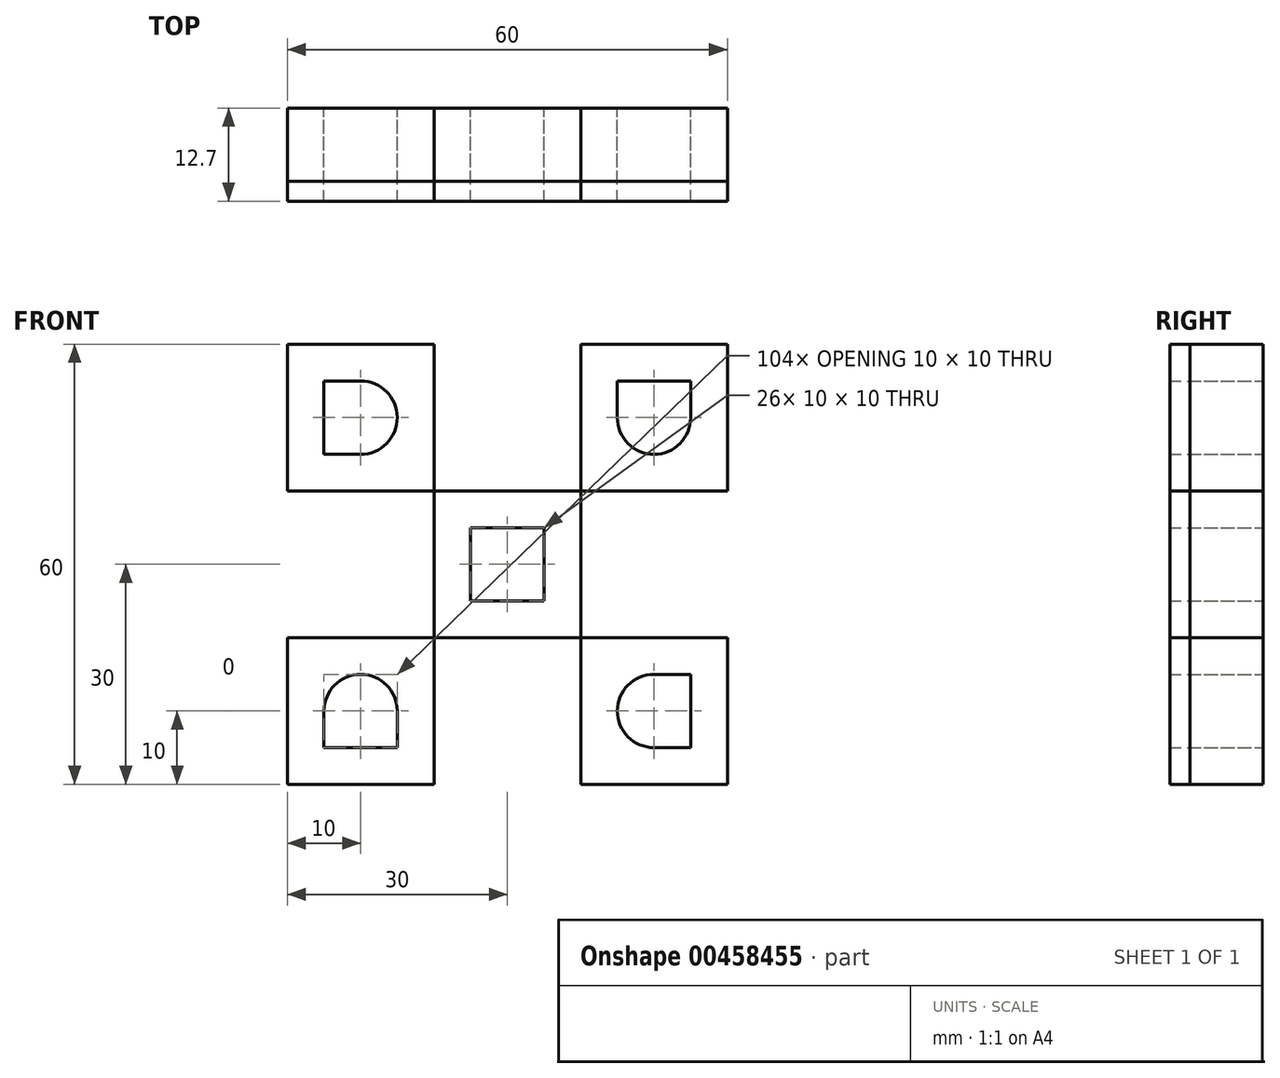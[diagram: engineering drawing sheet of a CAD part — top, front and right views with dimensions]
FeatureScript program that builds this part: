
annotation { "Feature Type Name" : "Feature", "Feature Type Description" : "" }
export const myFeature = defineFeature(function(context is Context, id is Id, definition is map)
    precondition{}
    {
        {
            var Q0;
            Q0=qCreatedBy(makeId("Front.planeOp"),FACE);
            var sketch = newSketch(context, id + "F0", { "sketchPlane" : qUnion([Q0])});
            skLineSegment(sketch, "E0.bottom", {"start": v(0, 0) * mm, "end": v(20, 0) * mm});
            skLineSegment(sketch, "E0.top", {"start": v(0, 20) * mm, "end": v(20, 20) * mm});
            skLineSegment(sketch, "E0.left", {"start": v(0, 0) * mm, "end": v(0, 20) * mm});
            skLineSegment(sketch, "E0.right", {"start": v(20, 0) * mm, "end": v(20, 20) * mm});
            skLineSegment(sketch, "E1.bottom", {"start": v(20, 20) * mm, "end": v(40, 20) * mm});
            skLineSegment(sketch, "E1.top", {"start": v(20, 40) * mm, "end": v(40, 40) * mm});
            skLineSegment(sketch, "E1.left", {"start": v(20, 20) * mm, "end": v(20, 40) * mm});
            skLineSegment(sketch, "E1.right", {"start": v(40, 20) * mm, "end": v(40, 40) * mm});
            skLineSegment(sketch, "E2.bottom", {"start": v(20, 0) * mm, "end": v(40, 0) * mm});
            skLineSegment(sketch, "E2.top", {"start": v(20, -20) * mm, "end": v(40, -20) * mm});
            skLineSegment(sketch, "E2.left", {"start": v(20, 0) * mm, "end": v(20, -20) * mm});
            skLineSegment(sketch, "E2.right", {"start": v(40, 0) * mm, "end": v(40, -20) * mm});
            skLineSegment(sketch, "E3.bottom", {"start": v(0, 0) * mm, "end": v(-20, 0) * mm});
            skLineSegment(sketch, "E3.top", {"start": v(0, -20) * mm, "end": v(-20, -20) * mm});
            skLineSegment(sketch, "E3.left", {"start": v(0, 0) * mm, "end": v(0, -20) * mm});
            skLineSegment(sketch, "E3.right", {"start": v(-20, 0) * mm, "end": v(-20, -20) * mm});
            skPoint(sketch, "E4.oppositeSnap0", {"position": v(30, 40) * mm});
            skLineSegment(sketch, "E4.bottom", {"start": v(0, 20) * mm, "end": v(-20, 20) * mm});
            skLineSegment(sketch, "E4.top", {"start": v(0, 40) * mm, "end": v(-20, 40) * mm});
            skLineSegment(sketch, "E4.left", {"start": v(0, 20) * mm, "end": v(0, 40) * mm});
            skLineSegment(sketch, "E4.right", {"start": v(-20, 20) * mm, "end": v(-20, 40) * mm});
            skLineSegment(sketch, "E5.bottom", {"start": v(15, 5) * mm, "end": v(5, 5) * mm});
            skLineSegment(sketch, "E5.top", {"start": v(15, 15) * mm, "end": v(5, 15) * mm});
            skLineSegment(sketch, "E5.left", {"start": v(15, 5) * mm, "end": v(15, 15) * mm});
            skLineSegment(sketch, "E5.right", {"start": v(5, 5) * mm, "end": v(5, 15) * mm});
            skPoint(sketch, "E5.middle", {"position": v(10, 10) * mm});
            skPoint(sketch, "E5.middle.positionSnap0", {"position": v(20, 10) * mm});
            skPoint(sketch, "E5.middle.positionSnap1", {"position": v(10, 20) * mm});
            skPoint(sketch, "E5.centerSnap0", {"position": v(20, 10) * mm});
            skPoint(sketch, "E5.centerSnap1", {"position": v(10, 20) * mm});
            skLineSegment(sketch, "E6.bottom", {"start": v(-10, 25) * mm, "end": v(-15, 25) * mm});
            skLineSegment(sketch, "E6.top", {"start": v(-10, 35) * mm, "end": v(-15, 35) * mm});
            skLineSegment(sketch, "E6.right", {"start": v(-15, 25) * mm, "end": v(-15, 35) * mm});
            skPoint(sketch, "E6.middle", {"position": v(-10, 30) * mm});
            skPoint(sketch, "E6.middle.positionSnap0", {"position": v(0, 30) * mm});
            skPoint(sketch, "E6.middle.positionSnap1", {"position": v(-10, 40) * mm});
            skPoint(sketch, "E6.centerSnap0", {"position": v(0, 30) * mm});
            skPoint(sketch, "E6.centerSnap1", {"position": v(-10, 40) * mm});
            skLineSegment(sketch, "E7.top", {"start": v(35, 35) * mm, "end": v(25, 35) * mm});
            skLineSegment(sketch, "E7.left", {"start": v(35, 30) * mm, "end": v(35, 35) * mm});
            skLineSegment(sketch, "E7.right", {"start": v(25, 30) * mm, "end": v(25, 35) * mm});
            skPoint(sketch, "E7.middle", {"position": v(30, 30) * mm});
            skPoint(sketch, "E7.middle.positionSnap0", {"position": v(40, 30) * mm});
            skPoint(sketch, "E7.centerSnap0", {"position": v(40, 30) * mm});
            skLineSegment(sketch, "E8.bottom", {"start": v(-5, -15) * mm, "end": v(-15, -15) * mm});
            skLineSegment(sketch, "E8.left", {"start": v(-5, -15) * mm, "end": v(-5, -10) * mm});
            skLineSegment(sketch, "E8.right", {"start": v(-15, -15) * mm, "end": v(-15, -10) * mm});
            skPoint(sketch, "E8.middle", {"position": v(-10, -10) * mm});
            skPoint(sketch, "E8.middle.positionSnap0", {"position": v(0, -10) * mm});
            skPoint(sketch, "E8.middle.positionSnap1", {"position": v(-10, 0) * mm});
            skPoint(sketch, "E8.centerSnap0", {"position": v(0, -10) * mm});
            skPoint(sketch, "E8.centerSnap1", {"position": v(-10, 0) * mm});
            skLineSegment(sketch, "E9.bottom", {"start": v(35, -15) * mm, "end": v(30, -15) * mm});
            skLineSegment(sketch, "E9.top", {"start": v(35, -5) * mm, "end": v(30, -5) * mm});
            skLineSegment(sketch, "E9.left", {"start": v(35, -15) * mm, "end": v(35, -5) * mm});
            skPoint(sketch, "E9.middle", {"position": v(30, -10) * mm});
            skPoint(sketch, "E9.middle.positionSnap0", {"position": v(40, -10) * mm});
            skPoint(sketch, "E9.middle.positionSnap1", {"position": v(30, 0) * mm});
            skPoint(sketch, "E9.centerSnap0", {"position": v(40, -10) * mm});
            skPoint(sketch, "E9.centerSnap1", {"position": v(30, 0) * mm});
            skArc(sketch, "E10", {"start": v(25, 30) * mm, "mid": v(30, 25) * mm, "end": v(35, 30) * mm});
            skArc(sketch, "E11", {"start": v(30, -5) * mm, "mid": v(25, -10) * mm, "end": v(30, -15) * mm});
            skArc(sketch, "E12", {"start": v(-5, -10) * mm, "mid": v(-10, -5) * mm, "end": v(-15, -10) * mm});
            skArc(sketch, "E13", {"start": v(-10, 25) * mm, "mid": v(-5, 30) * mm, "end": v(-10, 35) * mm});
            skCircle(sketch, "E14", {"center": v(10, 10) * mm, "radius": 5 * mm});
            skSolve(sketch);
        }
        {
            var Q0;
            Q0 = qSketchRegion(id + "F0", true);
            extrude(context, id + "F1", {"entities" : qUnion([Q0]), "depth" : 10 * mm});
        }
        {
            var Q0;
            Q0 = qSketchRegion(id + "F0", true);
            extrude(context, id + "F2", {"entities" : qUnion([Q0]), "depth" : 12.7 * mm});
        }
    });
